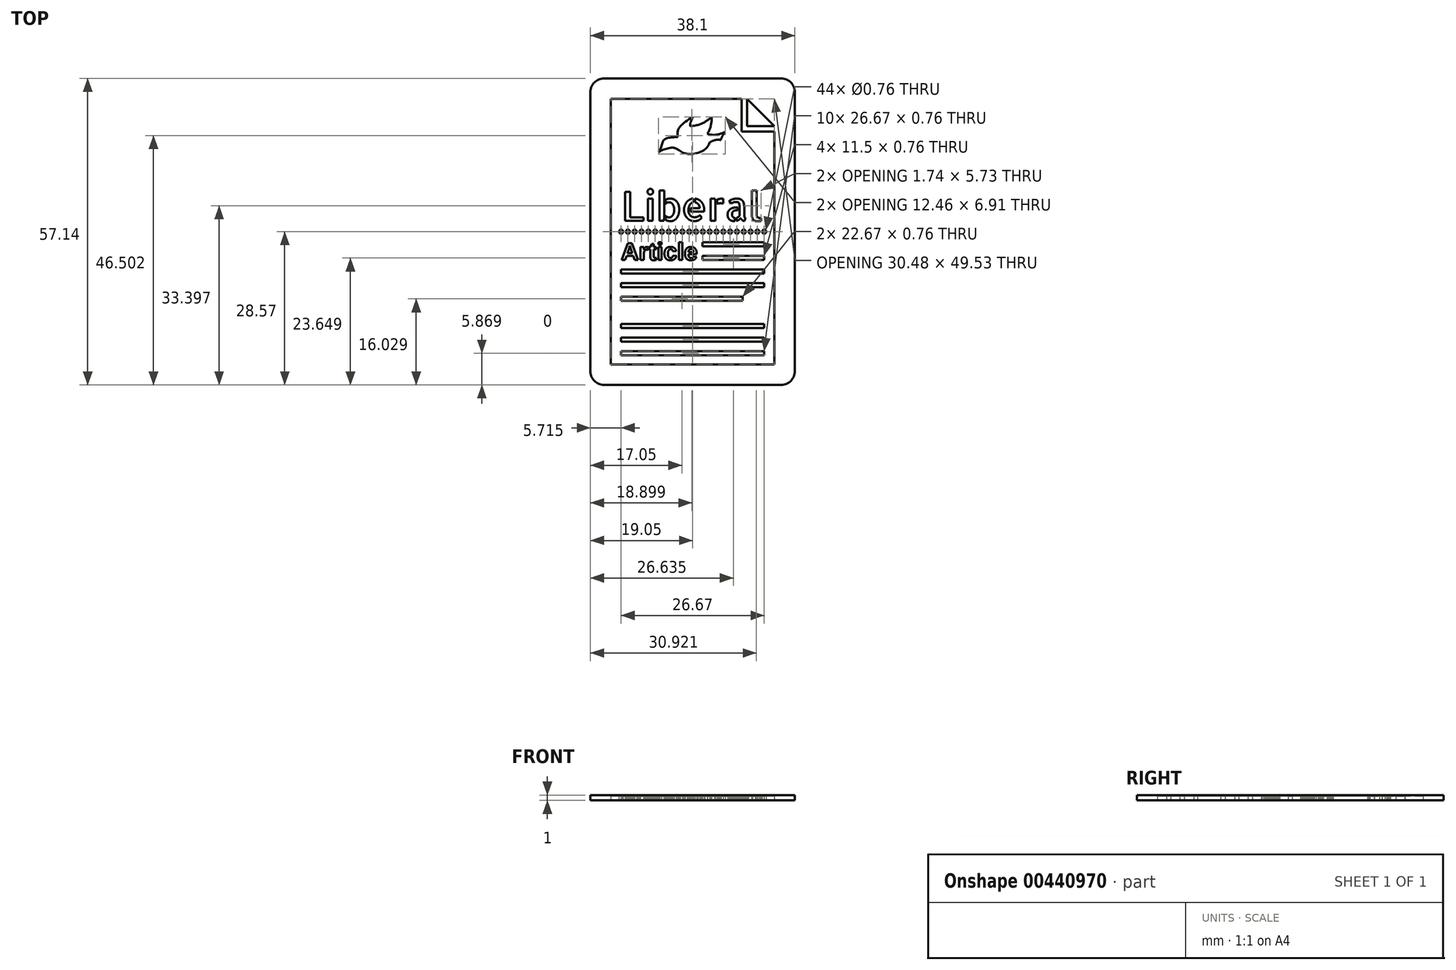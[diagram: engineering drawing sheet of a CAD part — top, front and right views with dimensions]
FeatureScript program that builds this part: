
annotation { "Feature Type Name" : "Feature", "Feature Type Description" : "" }
export const myFeature = defineFeature(function(context is Context, id is Id, definition is map)
    precondition{}
    {
        {
            var Q0;
            Q0=qCreatedBy(makeId("Top.planeOp"),FACE);
            var sketch = newSketch(context, id + "F0", { "sketchPlane" : qUnion([Q0])});
            skLineSegment(sketch, "E0.bottom", {"start": v(16.5, 28.58) * mm, "end": v(-16.51, 28.58) * mm});
            skLineSegment(sketch, "E0.top", {"start": v(16.51, -28.58) * mm, "end": v(-16.5, -28.58) * mm});
            skLineSegment(sketch, "E0.left", {"start": v(19.05, 26.04) * mm, "end": v(19.05, -26.04) * mm});
            skLineSegment(sketch, "E0.right", {"start": v(-19.05, 26.04) * mm, "end": v(-19.05, -26.04) * mm});
            skPoint(sketch, "E0.middle", {"position": v(0, 0) * mm});
            skPoint(sketch, "E1.visualSharp", {"position": v(-19.05, 28.58) * mm});
            skArc(sketch, "E1.filletArc", {"start": v(-16.51, 28.58) * mm, "mid": v(-18.3, 27.83) * mm, "end": v(-19.05, 26.04) * mm});
            skPoint(sketch, "E2.visualSharp", {"position": v(19.05, 28.58) * mm});
            skArc(sketch, "E2.filletArc", {"start": v(19.05, 26.04) * mm, "mid": v(18.3, 27.83) * mm, "end": v(16.5, 28.58) * mm});
            skPoint(sketch, "E3.visualSharp", {"position": v(19.05, -28.58) * mm});
            skArc(sketch, "E3.filletArc", {"start": v(16.51, -28.58) * mm, "mid": v(18.3, -27.83) * mm, "end": v(19.05, -26.04) * mm});
            skPoint(sketch, "E4.visualSharp", {"position": v(-19.05, -28.58) * mm});
            skArc(sketch, "E4.filletArc", {"start": v(-19.05, -26.04) * mm, "mid": v(-18.3, -27.83) * mm, "end": v(-16.5, -28.58) * mm});
            skLineSegment(sketch, "E5.bottom", {"start": v(9.14, 24.76) * mm, "end": v(-15.24, 24.76) * mm});
            skLineSegment(sketch, "E5.top", {"start": v(15.24, -24.77) * mm, "end": v(-15.24, -24.77) * mm});
            skLineSegment(sketch, "E5.left", {"start": v(15.24, 18.67) * mm, "end": v(15.24, -24.77) * mm});
            skLineSegment(sketch, "E5.right", {"start": v(-15.24, 24.77) * mm, "end": v(-15.24, -24.77) * mm});
            skLineSegment(sketch, "E6.top", {"start": v(15.24, 19.68) * mm, "end": v(10.16, 19.68) * mm});
            skLineSegment(sketch, "E6.right", {"start": v(10.16, 24.76) * mm, "end": v(10.16, 19.68) * mm});
            skLineSegment(sketch, "E7", {"start": v(10.16, 24.77) * mm, "end": v(15.24, 19.68) * mm});
            skPoint(sketch, "E8.orphan", {"position": v(15.24, 24.76) * mm});
            skLineSegment(sketch, "E9.0", {"start": v(15.24, 18.67) * mm, "end": v(9.14, 18.67) * mm});
            skLineSegment(sketch, "E9.1", {"start": v(9.14, 24.76) * mm, "end": v(9.14, 18.67) * mm});
            skText(sketch, "E10", { "text": "Liberal", "fontName": "AllertaStencil-Regular.ttf"});
            skCircle(sketch, "E11", {"center": v(-13.34, 0) * mm, "radius": 0.38 * mm});
            skPoint(sketch, "E11.centerSnap0", {"position": v(-15.24, 0) * mm});
            skCircle(sketch, "E12.1.0.0", {"center": v(-12.07, 0) * mm, "radius": 0.38 * mm});
            skCircle(sketch, "E12.2.0.0", {"center": v(-10.8, 0) * mm, "radius": 0.38 * mm});
            skCircle(sketch, "E12.3.0.0", {"center": v(-9.53, 0) * mm, "radius": 0.38 * mm});
            skCircle(sketch, "E12.4.0.0", {"center": v(-8.26, 0) * mm, "radius": 0.38 * mm});
            skCircle(sketch, "E12.5.0.0", {"center": v(-6.99, 0) * mm, "radius": 0.38 * mm});
            skCircle(sketch, "E12.6.0.0", {"center": v(-5.72, 0) * mm, "radius": 0.38 * mm});
            skCircle(sketch, "E12.7.0.0", {"center": v(-4.45, 0) * mm, "radius": 0.38 * mm});
            skCircle(sketch, "E12.8.0.0", {"center": v(-3.18, 0) * mm, "radius": 0.38 * mm});
            skCircle(sketch, "E12.9.0.0", {"center": v(-1.9, 0) * mm, "radius": 0.38 * mm});
            skCircle(sketch, "E12.10.0.0", {"center": v(-0.64, 0) * mm, "radius": 0.38 * mm});
            skCircle(sketch, "E12.11.0.0", {"center": v(0.63, 0) * mm, "radius": 0.38 * mm});
            skCircle(sketch, "E12.12.0.0", {"center": v(1.9, 0) * mm, "radius": 0.38 * mm});
            skCircle(sketch, "E12.13.0.0", {"center": v(3.17, 0) * mm, "radius": 0.38 * mm});
            skCircle(sketch, "E12.14.0.0", {"center": v(4.44, 0) * mm, "radius": 0.38 * mm});
            skCircle(sketch, "E12.15.0.0", {"center": v(5.71, 0) * mm, "radius": 0.38 * mm});
            skCircle(sketch, "E12.16.0.0", {"center": v(6.99, 0) * mm, "radius": 0.38 * mm});
            skCircle(sketch, "E12.17.0.0", {"center": v(8.26, 0) * mm, "radius": 0.38 * mm});
            skCircle(sketch, "E12.18.0.0", {"center": v(9.53, 0) * mm, "radius": 0.38 * mm});
            skCircle(sketch, "E12.19.0.0", {"center": v(10.8, 0) * mm, "radius": 0.38 * mm});
            skCircle(sketch, "E12.20.0.0", {"center": v(12.07, 0) * mm, "radius": 0.38 * mm});
            skCircle(sketch, "E12.21.0.0", {"center": v(13.34, 0) * mm, "radius": 0.38 * mm});
            skLineSegment(sketch, "E12.direction1", {"start": v(-13.34, 0) * mm, "end": v(-12.07, 0) * mm, "construction": true});
            skText(sketch, "E13", { "text": "Article", "fontName": "Arimo-Bold.ttf"});
            skLineSegment(sketch, "E14.bottom", {"start": v(1.84, -2) * mm, "end": v(13.34, -2) * mm});
            skLineSegment(sketch, "E14.top", {"start": v(1.84, -2.76) * mm, "end": v(13.34, -2.76) * mm});
            skLineSegment(sketch, "E14.left", {"start": v(1.84, -2) * mm, "end": v(1.84, -2.76) * mm});
            skLineSegment(sketch, "E14.right", {"start": v(13.34, -2) * mm, "end": v(13.34, -2.76) * mm});
            skLineSegment(sketch, "E15.bottom", {"start": v(1.84, -4.54) * mm, "end": v(13.34, -4.54) * mm});
            skLineSegment(sketch, "E15.top", {"start": v(1.84, -5.3) * mm, "end": v(13.34, -5.3) * mm});
            skLineSegment(sketch, "E15.left", {"start": v(1.84, -4.54) * mm, "end": v(1.84, -5.3) * mm});
            skLineSegment(sketch, "E15.right", {"start": v(13.34, -4.54) * mm, "end": v(13.34, -5.3) * mm});
            skLineSegment(sketch, "E16.bottom", {"start": v(-13.34, -7.08) * mm, "end": v(13.34, -7.08) * mm});
            skLineSegment(sketch, "E16.top", {"start": v(-13.34, -7.84) * mm, "end": v(13.34, -7.84) * mm});
            skLineSegment(sketch, "E16.left", {"start": v(-13.34, -7.08) * mm, "end": v(-13.34, -7.84) * mm});
            skLineSegment(sketch, "E16.right", {"start": v(13.34, -7.08) * mm, "end": v(13.34, -7.84) * mm});
            skLineSegment(sketch, "E17.bottom", {"start": v(-13.34, -9.62) * mm, "end": v(13.34, -9.62) * mm});
            skLineSegment(sketch, "E17.top", {"start": v(-13.34, -10.38) * mm, "end": v(13.34, -10.38) * mm});
            skLineSegment(sketch, "E17.left", {"start": v(-13.34, -9.62) * mm, "end": v(-13.34, -10.38) * mm});
            skLineSegment(sketch, "E17.right", {"start": v(13.34, -9.62) * mm, "end": v(13.34, -10.38) * mm});
            skLineSegment(sketch, "E18.bottom", {"start": v(-13.34, -12.16) * mm, "end": v(9.33, -12.16) * mm});
            skLineSegment(sketch, "E18.top", {"start": v(-13.34, -12.92) * mm, "end": v(9.33, -12.92) * mm});
            skLineSegment(sketch, "E18.left", {"start": v(-13.34, -12.16) * mm, "end": v(-13.34, -12.92) * mm});
            skLineSegment(sketch, "E18.right", {"start": v(9.33, -12.16) * mm, "end": v(9.33, -12.92) * mm});
            skLineSegment(sketch, "E19.bottom", {"start": v(-13.34, -19.78) * mm, "end": v(13.33, -19.78) * mm});
            skLineSegment(sketch, "E19.top", {"start": v(-13.34, -20.54) * mm, "end": v(13.33, -20.54) * mm});
            skLineSegment(sketch, "E19.left", {"start": v(-13.34, -19.78) * mm, "end": v(-13.34, -20.54) * mm});
            skLineSegment(sketch, "E19.right", {"start": v(13.34, -19.78) * mm, "end": v(13.34, -20.54) * mm});
            skLineSegment(sketch, "E20.bottom", {"start": v(-13.34, -22.32) * mm, "end": v(13.34, -22.32) * mm});
            skLineSegment(sketch, "E20.top", {"start": v(-13.34, -23.08) * mm, "end": v(13.34, -23.08) * mm});
            skLineSegment(sketch, "E20.left", {"start": v(-13.34, -22.32) * mm, "end": v(-13.34, -23.08) * mm});
            skLineSegment(sketch, "E20.right", {"start": v(13.34, -22.32) * mm, "end": v(13.34, -23.08) * mm});
            skLineSegment(sketch, "E21.bottom", {"start": v(-13.34, -17.24) * mm, "end": v(13.34, -17.24) * mm});
            skLineSegment(sketch, "E21.top", {"start": v(-13.34, -18) * mm, "end": v(13.34, -18) * mm});
            skLineSegment(sketch, "E21.left", {"start": v(-13.34, -17.24) * mm, "end": v(-13.34, -18) * mm});
            skLineSegment(sketch, "E21.right", {"start": v(13.34, -17.24) * mm, "end": v(13.34, -18) * mm});
            skEllipticalArc(sketch, "E22", {});
            skFitSpline(sketch, "E23", {"points": [v(-1.84, 14.74) * mm, v(-3.53, 15.64) * mm, v(-6.38, 14.89) * mm], "startDerivative": vector(-5.95, 3.68) * mm, "endDerivative": vector(-7.75, -3.47) * mm});
            skFitSpline(sketch, "E24", {"points": [v(-6.38, 14.89) * mm, v(-5.35, 17.13) * mm, v(-2.78, 17.66) * mm, v(-1.23, 18.05) * mm], "startDerivative": vector(6.83, 7.79) * mm, "endDerivative": vector(4.51, 2.6) * mm});
            skFitSpline(sketch, "E25", {"points": [v(-2.78, 17.66) * mm, v(0, 21.39) * mm], "startDerivative": vector(-0.11, 3.43) * mm, "endDerivative": vector(9.36, 5.61) * mm});
            skFitSpline(sketch, "E26", {"points": [v(3.5, 21.34) * mm, v(2.7, 18.26) * mm], "startDerivative": vector(0.54, -0.84) * mm, "endDerivative": vector(-2.09, -2.32) * mm});
            skFitSpline(sketch, "E27", {"points": [v(2.7, 18.26) * mm, v(6.08, 18.57) * mm], "startDerivative": vector(4.06, -1.31) * mm, "endDerivative": vector(3.72, 1.38) * mm});
            skFitSpline(sketch, "E28", {"points": [v(6.08, 18.57) * mm, v(5.22, 17.07) * mm], "startDerivative": vector(-1.24, -1.5) * mm, "endDerivative": vector(-0.53, -1.77) * mm});
            skFitSpline(sketch, "E29", {"points": [v(5.22, 17.07) * mm, v(3.17, 16.63) * mm], "startDerivative": vector(-2.12, 0.62) * mm, "endDerivative": vector(-1.68, -1.15) * mm});
            skFitSpline(sketch, "E30", {"points": [v(0, 21.39) * mm, v(-0.42, 19.66) * mm], "startDerivative": vector(-0.42, -1.72) * mm, "endDerivative": vector(0.66, -1.46) * mm});
            skFitSpline(sketch, "E31", {"points": [v(-0.42, 19.66) * mm, v(3.5, 21.34) * mm], "startDerivative": vector(6.18, 0.75) * mm, "endDerivative": vector(3.75, 2.97) * mm});
            const initialGuessF0  = {"E10": [-0.01324, 0.002, 1, 0, 0.0054], "E13": [-0.01334, -0.0053, 1, 0, 0.0033], "E22": [2.329519585648728e-06, 0.016765, -0.9848808836271908, -0.17323292142599894, 0.00325, 0.00225, 0.8405781417236297, 2.835182432077272]};
            skSetInitialGuess(sketch, initialGuessF0);
            skSolve(sketch);
        }
        {
            var Q0;
            Q0=qSketchRegion(id+"F0",true);
            var Q1;
            Q1=makeQuery(id+"F0.imprint","IMPRINT",FACE,{"disambiguationData":[TD([[makeQuery(id+"F0.imprint","IMPRINT",EDGE,{"derivedFrom":sQuery(id+"F0.wireOp",EDGE,"1hngZ8Vo-O2Y1-8GoF-9924-SmxzgvlIe6eu")}),1.0]])]});
            var Q2;
            Q2=makeQuery(id+"F0.imprint","IMPRINT",FACE,{"disambiguationData":[TD([[makeQuery(id+"F0.imprint","IMPRINT",EDGE,{"derivedFrom":sQuery(id+"F0.wireOp",EDGE,"v3mnc92D-8hCO-dKtl-YXU8-LdhrgQy31VMY")}),1.0]])]});
            var Q3;
            Q3=makeQuery(id+"F0.imprint","IMPRINT",FACE,{"disambiguationData":[TD([[makeQuery(id+"F0.imprint","IMPRINT",EDGE,{"derivedFrom":sQuery(id+"F0.wireOp",EDGE,"XZppkLhH-C5au-Wygf-dwhr-iVVlCesrx2pO")}),1.0]])]});
            var Q4;
            Q4=makeQuery(id+"F0.imprint","IMPRINT",FACE,{"disambiguationData":[TD([[makeQuery(id+"F0.imprint","IMPRINT",EDGE,{"derivedFrom":sQuery(id+"F0.wireOp",EDGE,"y07g3fre-KKaQ-oYPB-yLvA-0BrsEIY3R70T")}),1.0]])]});
            var Q5;
            Q5=makeQuery(id+"F0.imprint","IMPRINT",FACE,{"disambiguationData":[TD([[makeQuery(id+"F0.imprint","IMPRINT",EDGE,{"derivedFrom":sQuery(id+"F0.wireOp",EDGE,"E10.sketch_text.stroke-0")}),-1.0]])]});
            var Q6;
            Q6=makeQuery(id+"F0.imprint","IMPRINT",FACE,{"disambiguationData":[TD([[makeQuery(id+"F0.imprint","IMPRINT",EDGE,{"derivedFrom":sQuery(id+"F0.wireOp",EDGE,"E10.sketch_text.stroke-8")}),-1.0]])]});
            var Q7;
            Q7=makeQuery(id+"F0.imprint","IMPRINT",FACE,{"disambiguationData":[TD([[makeQuery(id+"F0.imprint","IMPRINT",EDGE,{"derivedFrom":sQuery(id+"F0.wireOp",EDGE,"E10.sketch_text.stroke-4")}),-1.0]])]});
            var Q8;
            Q8=makeQuery(id+"F0.imprint","IMPRINT",FACE,{"disambiguationData":[TD([[makeQuery(id+"F0.imprint","IMPRINT",EDGE,{"derivedFrom":sQuery(id+"F0.wireOp",EDGE,"E10.sketch_text.stroke-31")}),-1.0]])]});
            var Q9;
            Q9=makeQuery(id+"F0.imprint","IMPRINT",FACE,{"disambiguationData":[TD([[makeQuery(id+"F0.imprint","IMPRINT",EDGE,{"derivedFrom":sQuery(id+"F0.wireOp",EDGE,"E10.sketch_text.stroke-12")}),-1.0]])]});
            var Q10;
            Q10=makeQuery(id+"F0.imprint","IMPRINT",FACE,{"disambiguationData":[TD([[makeQuery(id+"F0.imprint","IMPRINT",EDGE,{"derivedFrom":sQuery(id+"F0.wireOp",EDGE,"E10.sketch_text.stroke-96")}),-1.0]])]});
            var Q11;
            Q11=makeQuery(id+"F0.imprint","IMPRINT",FACE,{"disambiguationData":[TD([[makeQuery(id+"F0.imprint","IMPRINT",EDGE,{"derivedFrom":sQuery(id+"F0.wireOp",EDGE,"E10.sketch_text.stroke-87")}),-1.0]])]});
            var Q12;
            Q12=makeQuery(id+"F0.imprint","IMPRINT",FACE,{"disambiguationData":[TD([[makeQuery(id+"F0.imprint","IMPRINT",EDGE,{"derivedFrom":sQuery(id+"F0.wireOp",EDGE,"E10.sketch_text.stroke-67")}),-1.0]])]});
            var Q13;
            Q13=makeQuery(id+"F0.imprint","IMPRINT",FACE,{"disambiguationData":[TD([[makeQuery(id+"F0.imprint","IMPRINT",EDGE,{"derivedFrom":sQuery(id+"F0.wireOp",EDGE,"E10.sketch_text.stroke-81")}),-1.0]])]});
            var Q14;
            Q14=makeQuery(id+"F0.imprint","IMPRINT",FACE,{"disambiguationData":[TD([[makeQuery(id+"F0.imprint","IMPRINT",EDGE,{"derivedFrom":sQuery(id+"F0.wireOp",EDGE,"E10.sketch_text.stroke-116")}),-1.0]])]});
            var Q15;
            Q15=makeQuery(id+"F0.imprint","IMPRINT",FACE,{"disambiguationData":[TD([[makeQuery(id+"F0.imprint","IMPRINT",EDGE,{"derivedFrom":sQuery(id+"F0.wireOp",EDGE,"E10.sketch_text.stroke-122")}),-1.0]])]});
            var Q16;
            Q16=makeQuery(id+"F0.imprint","IMPRINT",FACE,{"disambiguationData":[TD([[makeQuery(id+"F0.imprint","IMPRINT",EDGE,{"derivedFrom":sQuery(id+"F0.wireOp",EDGE,"E10.sketch_text.stroke-110")}),-1.0]])]});
            var Q17;
            Q17=makeQuery(id+"F0.imprint","IMPRINT",FACE,{"disambiguationData":[TD([[makeQuery(id+"F0.imprint","IMPRINT",EDGE,{"derivedFrom":sQuery(id+"F0.wireOp",EDGE,"E10.sketch_text.stroke-142")}),-1.0]])]});
            var Q18;
            Q18=makeQuery(id+"F0.imprint","IMPRINT",FACE,{"disambiguationData":[TD([[makeQuery(id+"F0.imprint","IMPRINT",EDGE,{"derivedFrom":sQuery(id+"F0.wireOp",EDGE,"E10.sketch_text.stroke-138")}),-1.0]])]});
            var Q19;
            Q19=makeQuery(id+"F0.imprint","IMPRINT",FACE,{"disambiguationData":[TD([[makeQuery(id+"F0.imprint","IMPRINT",EDGE,{"derivedFrom":sQuery(id+"F0.wireOp",EDGE,"E10.sketch_text.stroke-170")}),-1.0]])]});
            var Q20;
            Q20=makeQuery(id+"F0.imprint","IMPRINT",FACE,{"disambiguationData":[TD([[makeQuery(id+"F0.imprint","IMPRINT",EDGE,{"derivedFrom":sQuery(id+"F0.wireOp",EDGE,"E10.sketch_text.stroke-179")}),-1.0]])]});
            var Q21;
            Q21=makeQuery(id+"F0.imprint","IMPRINT",FACE,{"disambiguationData":[TD([[makeQuery(id+"F0.imprint","IMPRINT",EDGE,{"derivedFrom":sQuery(id+"F0.wireOp",EDGE,"E10.sketch_text.stroke-150")}),-1.0]])]});
            var Q22;
            Q22=makeQuery(id+"F0.imprint","IMPRINT",FACE,{"disambiguationData":[TD([[makeQuery(id+"F0.imprint","IMPRINT",EDGE,{"derivedFrom":sQuery(id+"F0.wireOp",EDGE,"E10.sketch_text.stroke-164")}),-1.0]])]});
            var Q23;
            Q23=makeQuery(id+"F0.imprint","IMPRINT",FACE,{"disambiguationData":[TD([[makeQuery(id+"F0.imprint","IMPRINT",EDGE,{"derivedFrom":sQuery(id+"F0.wireOp",EDGE,"E10.sketch_text.stroke-193")}),-1.0]])]});
            var Q24;
            Q24=makeQuery(id+"F0.imprint","IMPRINT",FACE,{"disambiguationData":[TD([[makeQuery(id+"F0.imprint","IMPRINT",EDGE,{"derivedFrom":sQuery(id+"F0.wireOp",EDGE,"E11")}),1.0]])]});
            var Q25;
            Q25=makeQuery(id+"F0.imprint","IMPRINT",FACE,{"disambiguationData":[TD([[makeQuery(id+"F0.imprint","IMPRINT",EDGE,{"derivedFrom":sQuery(id+"F0.wireOp",EDGE,"E12.1.0.0")}),1.0]])]});
            var Q26;
            Q26=makeQuery(id+"F0.imprint","IMPRINT",FACE,{"disambiguationData":[TD([[makeQuery(id+"F0.imprint","IMPRINT",EDGE,{"derivedFrom":sQuery(id+"F0.wireOp",EDGE,"E12.2.0.0")}),1.0]])]});
            var Q27;
            Q27=makeQuery(id+"F0.imprint","IMPRINT",FACE,{"disambiguationData":[TD([[makeQuery(id+"F0.imprint","IMPRINT",EDGE,{"derivedFrom":sQuery(id+"F0.wireOp",EDGE,"E12.3.0.0")}),1.0]])]});
            var Q28;
            Q28=makeQuery(id+"F0.imprint","IMPRINT",FACE,{"disambiguationData":[TD([[makeQuery(id+"F0.imprint","IMPRINT",EDGE,{"derivedFrom":sQuery(id+"F0.wireOp",EDGE,"E12.4.0.0")}),1.0]])]});
            var Q29;
            Q29=makeQuery(id+"F0.imprint","IMPRINT",FACE,{"disambiguationData":[TD([[makeQuery(id+"F0.imprint","IMPRINT",EDGE,{"derivedFrom":sQuery(id+"F0.wireOp",EDGE,"E12.5.0.0")}),1.0]])]});
            var Q30;
            Q30=makeQuery(id+"F0.imprint","IMPRINT",FACE,{"disambiguationData":[TD([[makeQuery(id+"F0.imprint","IMPRINT",EDGE,{"derivedFrom":sQuery(id+"F0.wireOp",EDGE,"E12.6.0.0")}),1.0]])]});
            var Q31;
            Q31=makeQuery(id+"F0.imprint","IMPRINT",FACE,{"disambiguationData":[TD([[makeQuery(id+"F0.imprint","IMPRINT",EDGE,{"derivedFrom":sQuery(id+"F0.wireOp",EDGE,"E12.7.0.0")}),1.0]])]});
            var Q32;
            Q32=makeQuery(id+"F0.imprint","IMPRINT",FACE,{"disambiguationData":[TD([[makeQuery(id+"F0.imprint","IMPRINT",EDGE,{"derivedFrom":sQuery(id+"F0.wireOp",EDGE,"E12.8.0.0")}),1.0]])]});
            var Q33;
            Q33=makeQuery(id+"F0.imprint","IMPRINT",FACE,{"disambiguationData":[TD([[makeQuery(id+"F0.imprint","IMPRINT",EDGE,{"derivedFrom":sQuery(id+"F0.wireOp",EDGE,"E12.9.0.0")}),1.0]])]});
            var Q34;
            Q34=makeQuery(id+"F0.imprint","IMPRINT",FACE,{"disambiguationData":[TD([[makeQuery(id+"F0.imprint","IMPRINT",EDGE,{"derivedFrom":sQuery(id+"F0.wireOp",EDGE,"E12.10.0.0")}),1.0]])]});
            var Q35;
            Q35=makeQuery(id+"F0.imprint","IMPRINT",FACE,{"disambiguationData":[TD([[makeQuery(id+"F0.imprint","IMPRINT",EDGE,{"derivedFrom":sQuery(id+"F0.wireOp",EDGE,"E12.11.0.0")}),1.0]])]});
            var Q36;
            Q36=makeQuery(id+"F0.imprint","IMPRINT",FACE,{"disambiguationData":[TD([[makeQuery(id+"F0.imprint","IMPRINT",EDGE,{"derivedFrom":sQuery(id+"F0.wireOp",EDGE,"E12.12.0.0")}),1.0]])]});
            var Q37;
            Q37=makeQuery(id+"F0.imprint","IMPRINT",FACE,{"disambiguationData":[TD([[makeQuery(id+"F0.imprint","IMPRINT",EDGE,{"derivedFrom":sQuery(id+"F0.wireOp",EDGE,"E12.13.0.0")}),1.0]])]});
            var Q38;
            Q38=makeQuery(id+"F0.imprint","IMPRINT",FACE,{"disambiguationData":[TD([[makeQuery(id+"F0.imprint","IMPRINT",EDGE,{"derivedFrom":sQuery(id+"F0.wireOp",EDGE,"E12.14.0.0")}),1.0]])]});
            var Q39;
            Q39=makeQuery(id+"F0.imprint","IMPRINT",FACE,{"disambiguationData":[TD([[makeQuery(id+"F0.imprint","IMPRINT",EDGE,{"derivedFrom":sQuery(id+"F0.wireOp",EDGE,"E12.15.0.0")}),1.0]])]});
            var Q40;
            Q40=makeQuery(id+"F0.imprint","IMPRINT",FACE,{"disambiguationData":[TD([[makeQuery(id+"F0.imprint","IMPRINT",EDGE,{"derivedFrom":sQuery(id+"F0.wireOp",EDGE,"E12.16.0.0")}),1.0]])]});
            var Q41;
            Q41=makeQuery(id+"F0.imprint","IMPRINT",FACE,{"disambiguationData":[TD([[makeQuery(id+"F0.imprint","IMPRINT",EDGE,{"derivedFrom":sQuery(id+"F0.wireOp",EDGE,"E12.17.0.0")}),1.0]])]});
            var Q42;
            Q42=makeQuery(id+"F0.imprint","IMPRINT",FACE,{"disambiguationData":[TD([[makeQuery(id+"F0.imprint","IMPRINT",EDGE,{"derivedFrom":sQuery(id+"F0.wireOp",EDGE,"E12.18.0.0")}),1.0]])]});
            var Q43;
            Q43=makeQuery(id+"F0.imprint","IMPRINT",FACE,{"disambiguationData":[TD([[makeQuery(id+"F0.imprint","IMPRINT",EDGE,{"derivedFrom":sQuery(id+"F0.wireOp",EDGE,"E12.19.0.0")}),1.0]])]});
            var Q44;
            Q44=makeQuery(id+"F0.imprint","IMPRINT",FACE,{"disambiguationData":[TD([[makeQuery(id+"F0.imprint","IMPRINT",EDGE,{"derivedFrom":sQuery(id+"F0.wireOp",EDGE,"E12.20.0.0")}),1.0]])]});
            var Q45;
            Q45=makeQuery(id+"F0.imprint","IMPRINT",FACE,{"disambiguationData":[TD([[makeQuery(id+"F0.imprint","IMPRINT",EDGE,{"derivedFrom":sQuery(id+"F0.wireOp",EDGE,"E12.21.0.0")}),1.0]])]});
            var Q46;
            Q46=makeQuery(id+"F0.imprint","IMPRINT",FACE,{"disambiguationData":[TD([[makeQuery(id+"F0.imprint","IMPRINT",EDGE,{"derivedFrom":sQuery(id+"F0.wireOp",EDGE,"E13.sketch_text.stroke-0")}),-1.0]])]});
            var Q47;
            Q47=makeQuery(id+"F0.imprint","IMPRINT",FACE,{"disambiguationData":[TD([[makeQuery(id+"F0.imprint","IMPRINT",EDGE,{"derivedFrom":sQuery(id+"F0.wireOp",EDGE,"E13.sketch_text.stroke-15")}),-1.0]])]});
            var Q48;
            Q48=makeQuery(id+"F0.imprint","IMPRINT",FACE,{"disambiguationData":[TD([[makeQuery(id+"F0.imprint","IMPRINT",EDGE,{"derivedFrom":sQuery(id+"F0.wireOp",EDGE,"E13.sketch_text.stroke-32")}),-1.0]])]});
            var Q49;
            Q49=makeQuery(id+"F0.imprint","IMPRINT",FACE,{"disambiguationData":[TD([[makeQuery(id+"F0.imprint","IMPRINT",EDGE,{"derivedFrom":sQuery(id+"F0.wireOp",EDGE,"E13.sketch_text.stroke-54")}),-1.0]])]});
            var Q50;
            Q50=makeQuery(id+"F0.imprint","IMPRINT",FACE,{"disambiguationData":[TD([[makeQuery(id+"F0.imprint","IMPRINT",EDGE,{"derivedFrom":sQuery(id+"F0.wireOp",EDGE,"E13.sketch_text.stroke-50")}),-1.0]])]});
            var Q51;
            Q51=makeQuery(id+"F0.imprint","IMPRINT",FACE,{"disambiguationData":[TD([[makeQuery(id+"F0.imprint","IMPRINT",EDGE,{"derivedFrom":sQuery(id+"F0.wireOp",EDGE,"E13.sketch_text.stroke-58")}),-1.0]])]});
            var Q52;
            Q52=makeQuery(id+"F0.imprint","IMPRINT",FACE,{"disambiguationData":[TD([[makeQuery(id+"F0.imprint","IMPRINT",EDGE,{"derivedFrom":sQuery(id+"F0.wireOp",EDGE,"E13.sketch_text.stroke-75")}),-1.0]])]});
            var Q53;
            Q53=makeQuery(id+"F0.imprint","IMPRINT",FACE,{"disambiguationData":[TD([[makeQuery(id+"F0.imprint","IMPRINT",EDGE,{"derivedFrom":sQuery(id+"F0.wireOp",EDGE,"E13.sketch_text.stroke-79")}),-1.0]])]});
            var Q54;
            Q54=makeQuery(id+"F0.imprint","IMPRINT",FACE,{"disambiguationData":[TD([[makeQuery(id+"F0.imprint","IMPRINT",EDGE,{"derivedFrom":sQuery(id+"F0.wireOp",EDGE,"E14.bottom")}),-1.0]])]});
            var Q55;
            Q55=makeQuery(id+"F0.imprint","IMPRINT",FACE,{"disambiguationData":[TD([[makeQuery(id+"F0.imprint","IMPRINT",EDGE,{"derivedFrom":sQuery(id+"F0.wireOp",EDGE,"E15.bottom")}),-1.0]])]});
            var Q56;
            Q56=makeQuery(id+"F0.imprint","IMPRINT",FACE,{"disambiguationData":[TD([[makeQuery(id+"F0.imprint","IMPRINT",EDGE,{"derivedFrom":sQuery(id+"F0.wireOp",EDGE,"E16.bottom")}),-1.0]])]});
            var Q57;
            Q57=makeQuery(id+"F0.imprint","IMPRINT",FACE,{"disambiguationData":[TD([[makeQuery(id+"F0.imprint","IMPRINT",EDGE,{"derivedFrom":sQuery(id+"F0.wireOp",EDGE,"E17.bottom")}),-1.0]])]});
            var Q58;
            Q58=makeQuery(id+"F0.imprint","IMPRINT",FACE,{"disambiguationData":[TD([[makeQuery(id+"F0.imprint","IMPRINT",EDGE,{"derivedFrom":sQuery(id+"F0.wireOp",EDGE,"E18.bottom")}),-1.0]])]});
            var Q59;
            Q59=makeQuery(id+"F0.imprint","IMPRINT",FACE,{"disambiguationData":[TD([[makeQuery(id+"F0.imprint","IMPRINT",EDGE,{"derivedFrom":sQuery(id+"F0.wireOp",EDGE,"E21.bottom")}),-1.0]])]});
            var Q60;
            Q60=makeQuery(id+"F0.imprint","IMPRINT",FACE,{"disambiguationData":[TD([[makeQuery(id+"F0.imprint","IMPRINT",EDGE,{"derivedFrom":sQuery(id+"F0.wireOp",EDGE,"E19.bottom")}),-1.0]])]});
            var Q61;
            Q61=makeQuery(id+"F0.imprint","IMPRINT",FACE,{"disambiguationData":[TD([[makeQuery(id+"F0.imprint","IMPRINT",EDGE,{"derivedFrom":sQuery(id+"F0.wireOp",EDGE,"E20.bottom")}),-1.0]])]});
            var Q62;
            Q62=makeQuery(id+"F0.imprint","IMPRINT",FACE,{"disambiguationData":[TD([[makeQuery(id+"F0.imprint","IMPRINT",EDGE,{"derivedFrom":sQuery(id+"F0.wireOp",EDGE,"E10.sketch_text.stroke-18")}),-1.0]])]});
            var Q63;
            Q63=makeQuery(id+"F0.imprint","IMPRINT",FACE,{"disambiguationData":[TD([[makeQuery(id+"F0.imprint","IMPRINT",EDGE,{"derivedFrom":sQuery(id+"F0.wireOp",EDGE,"E10.sketch_text.stroke-88")}),-1.0]])]});
            var Q64;
            Q64=makeQuery(id+"F0.imprint","IMPRINT",FACE,{"disambiguationData":[TD([[makeQuery(id+"F0.imprint","IMPRINT",EDGE,{"derivedFrom":sQuery(id+"F0.wireOp",EDGE,"E10.sketch_text.stroke-51")}),-1.0]])]});
            var Q65;
            Q65=makeQuery(id+"F0.imprint","IMPRINT",FACE,{"disambiguationData":[TD([[makeQuery(id+"F0.imprint","IMPRINT",EDGE,{"derivedFrom":sQuery(id+"F0.wireOp",EDGE,"E22")}),1.0]])]});
            extrude(context, id + "F1", {"entities" : qUnion([Q0, Q1, Q2, Q3, Q4, Q5, Q6, Q7, Q8, Q9, Q10, Q11, Q12, Q13, Q14, Q15, Q16, Q17, Q18, Q19, Q20, Q21, Q22, Q23, Q24, Q25, Q26, Q27, Q28, Q29, Q30, Q31, Q32, Q33, Q34, Q35, Q36, Q37, Q38, Q39, Q40, Q41, Q42, Q43, Q44, Q45, Q46, Q47, Q48, Q49, Q50, Q51, Q52, Q53, Q54, Q55, Q56, Q57, Q58, Q59, Q60, Q61, Q62, Q63, Q64, Q65]), "depth" : 1 * mm});
        }
        {
            var Q0;
            Q0=makeQuery(id+"F0.imprint","IMPRINT",FACE,{"disambiguationData":[TD([[makeQuery(id+"F0.imprint","IMPRINT",EDGE,{"derivedFrom":sQuery(id+"F0.wireOp",EDGE,"XZppkLhH-C5au-Wygf-dwhr-iVVlCesrx2pO")}),-1.0]])]});
            var Q1;
            Q1=makeQuery(id+"F0.imprint","IMPRINT",FACE,{"disambiguationData":[TD([[makeQuery(id+"F0.imprint","IMPRINT",EDGE,{"derivedFrom":sQuery(id+"F0.wireOp",EDGE,"E6.top")}),-1.0]])]});
            var Q2;
            Q2=makeQuery(id+"F0.imprint","IMPRINT",FACE,{"disambiguationData":[TD([[makeQuery(id+"F0.imprint","IMPRINT",EDGE,{"derivedFrom":sQuery(id+"F0.wireOp",EDGE,"E5.bottom")}),1.0]])]});
            var Q3;
            Q3=makeQuery(id+"F0.imprint","IMPRINT",FACE,{"disambiguationData":[TD([[makeQuery(id+"F0.imprint","IMPRINT",EDGE,{"derivedFrom":sQuery(id+"F0.wireOp",EDGE,"E13.sketch_text.stroke-8")}),1.0]])]});
            var Q4;
            Q4=makeQuery(id+"F0.imprint","IMPRINT",FACE,{"disambiguationData":[TD([[makeQuery(id+"F0.imprint","IMPRINT",EDGE,{"derivedFrom":sQuery(id+"F0.wireOp",EDGE,"E13.sketch_text.stroke-92")}),1.0]])]});
            extrude(context, id + "F2", {"entities" : qUnion([Q0, Q1, Q2, Q3, Q4]), "depth" : .8 * mm});
        }
        {
            var Q0;
            Q0=makeQuery(id+"F0.imprint","IMPRINT",FACE,{"disambiguationData":[TD([[makeQuery(id+"F0.imprint","IMPRINT",EDGE,{"derivedFrom":sQuery(id+"F0.wireOp",EDGE,"E5.bottom")}),1.0]])]});
            var Q1;
            Q1=makeQuery(id+"F0.imprint","IMPRINT",FACE,{"disambiguationData":[TD([[makeQuery(id+"F0.imprint","IMPRINT",EDGE,{"derivedFrom":sQuery(id+"F0.wireOp",EDGE,"XZppkLhH-C5au-Wygf-dwhr-iVVlCesrx2pO")}),-1.0]])]});
            var Q2;
            Q2=makeQuery(id+"F0.imprint","IMPRINT",FACE,{"disambiguationData":[TD([[makeQuery(id+"F0.imprint","IMPRINT",EDGE,{"derivedFrom":sQuery(id+"F0.wireOp",EDGE,"E6.top")}),-1.0]])]});
            var Q3;
            Q3=makeQuery(id+"F0.imprint","IMPRINT",FACE,{"disambiguationData":[TD([[makeQuery(id+"F0.imprint","IMPRINT",EDGE,{"derivedFrom":sQuery(id+"F0.wireOp",EDGE,"E13.sketch_text.stroke-8")}),1.0]])]});
            var Q4;
            Q4=makeQuery(id+"F0.imprint","IMPRINT",FACE,{"disambiguationData":[TD([[makeQuery(id+"F0.imprint","IMPRINT",EDGE,{"derivedFrom":sQuery(id+"F0.wireOp",EDGE,"E13.sketch_text.stroke-92")}),1.0]])]});
            extrude(context, id + "F3", {"entities" : qUnion([Q0, Q1, Q2, Q3, Q4]), "depth" : 1 * mm, "hasSecondDirection" : true, "secondDirectionOppositeDirection" : true, "secondDirectionDepth" : -.8 * mm});
        }
    });
